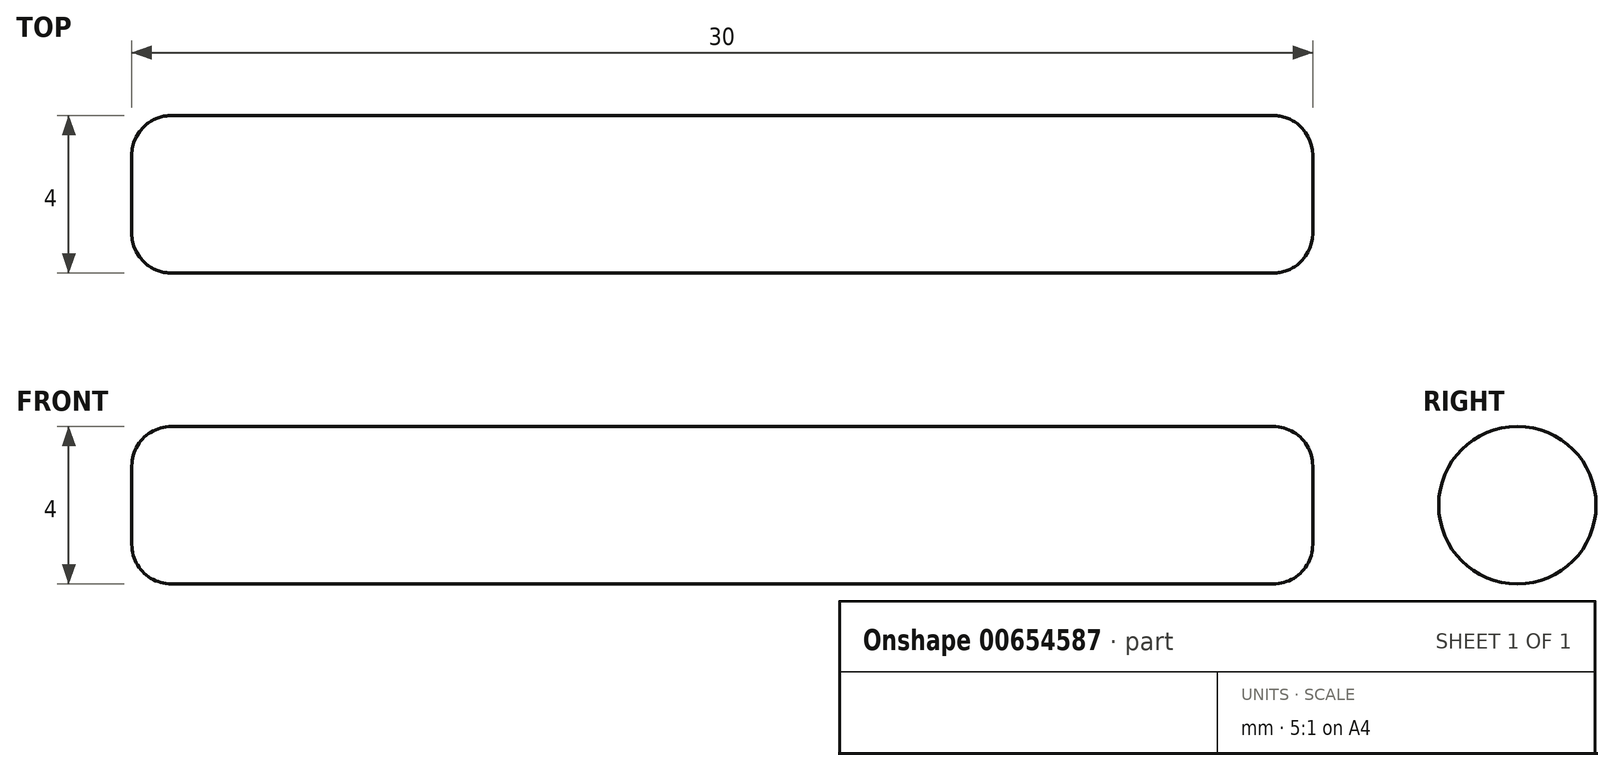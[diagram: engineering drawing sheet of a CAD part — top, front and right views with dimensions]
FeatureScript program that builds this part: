
annotation { "Feature Type Name" : "Feature", "Feature Type Description" : "" }
export const myFeature = defineFeature(function(context is Context, id is Id, definition is map)
    precondition{}
    {
        {
            var Q0;
            Q0=qCreatedBy(makeId("Front.planeOp"),FACE);
            var sketch = newSketch(context, id + "F0", { "sketchPlane" : qUnion([Q0])});
            skLineSegment(sketch, "E0.bottom", {"start": v(0, 0) * mm, "end": v(30, 0) * mm});
            skLineSegment(sketch, "E0.top", {"start": v(0, 2) * mm, "end": v(30, 2) * mm});
            skLineSegment(sketch, "E0.left", {"start": v(0, 0) * mm, "end": v(0, 2) * mm});
            skLineSegment(sketch, "E0.right", {"start": v(30, 0) * mm, "end": v(30, 2) * mm});
            skSolve(sketch);
        }
        {
            var Q0;
            Q0=makeQuery(id+"F0.imprint","IMPRINT",FACE,{"disambiguationData":[TD([[makeQuery(id+"F0.imprint","IMPRINT",EDGE,{"derivedFrom":sQuery(id+"F0.wireOp",EDGE,"E0.bottom")}),1.0]])]});
            var Q1;
            Q1=sQuery(id+"F0.wireOp",EDGE,"E0.bottom");
            revolve(context, id + "F1", {"surfaceOperationType" : NewSurfaceOperationType.NEW, "entities" : qUnion([Q0]), "axis" : qUnion([Q1]), "revolveType" : RevolveType.FULL});
        }
        {
            var Q0;
            Q0=makeQuery(id+"F1.opRevolve","SWEPT_EDGE",EDGE,{"disambiguationData":[OSD([sQuery(id+"F0.wireOp",EDGE,"E0.top"),sQuery(id+"F0.wireOp",EDGE,"E0.right")])]});
            var Q1;
            Q1=makeQuery(id+"F1.opRevolve","SWEPT_EDGE",EDGE,{"disambiguationData":[OSD([sQuery(id+"F0.wireOp",EDGE,"E0.top"),sQuery(id+"F0.wireOp",EDGE,"E0.left")])]});
            fillet(context, id + "F2", {"entities" : qUnion([Q0, Q1]), "tangentPropagation" : true, "radius" : 1 * mm, "defaultsChanged" : true, "vertexSettings" : [], "allowEdgeOverflow" : false});
        }
    });
